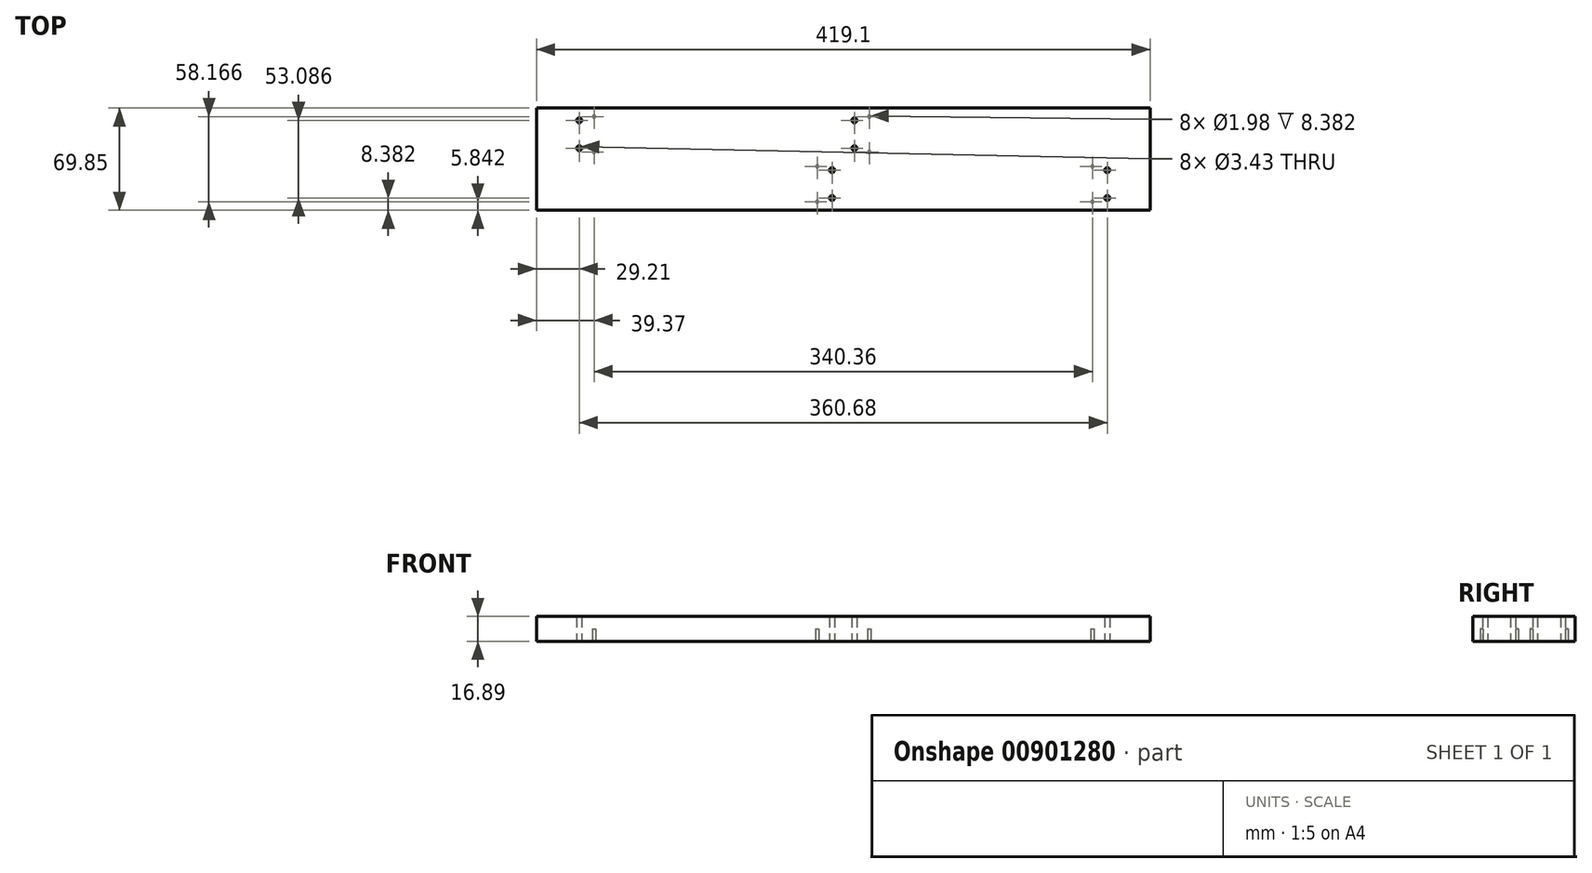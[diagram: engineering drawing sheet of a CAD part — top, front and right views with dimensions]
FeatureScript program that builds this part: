
annotation { "Feature Type Name" : "Feature", "Feature Type Description" : "" }
export const myFeature = defineFeature(function(context is Context, id is Id, definition is map)
    precondition{}
    {
        {
            var Q0;
            Q0=qCreatedBy(makeId("Top.planeOp"),FACE);
            var sketch = newSketch(context, id + "F0", { "sketchPlane" : qUnion([Q0])});
            skLineSegment(sketch, "E0.bottom", {"start": v(0, 0) * mm, "end": v(419.1, 0) * mm});
            skLineSegment(sketch, "E0.top", {"start": v(0, 69.85) * mm, "end": v(419.1, 69.85) * mm});
            skLineSegment(sketch, "E0.left", {"start": v(0, 0) * mm, "end": v(0, 69.85) * mm});
            skLineSegment(sketch, "E0.right", {"start": v(419.1, 0) * mm, "end": v(419.1, 69.85) * mm});
            skSolve(sketch);
        }
        {
            var Q0;
            Q0=qSketchRegion(id+"F0",true);
            extrude(context, id + "F1", {"entities" : qUnion([Q0]), "depth" : 16.9 * mm, "offsetDistance" : 25.4 * mm});
        }
        {
            var Q0;
            Q0=makeQuery(id+"F1.opExtrude","CAP_FACE",FACE,{"disambiguationData":[OSD([sQuery(id+"F0.wireOp",EDGE,"E0.bottom"),sQuery(id+"F0.wireOp",EDGE,"E0.top"),sQuery(id+"F0.wireOp",EDGE,"E0.left"),sQuery(id+"F0.wireOp",EDGE,"E0.right")])],"isStart":true});
            var sketch = newSketch(context, id + "F2", { "sketchPlane" : qUnion([Q0])});
            skCircle(sketch, "E1", {"center": v(379.73, -5.84) * mm, "radius": 1 * mm});
            skCircle(sketch, "E2", {"center": v(379.73, -29.97) * mm, "radius": 1 * mm});
            skCircle(sketch, "E3", {"center": v(227.33, -39.88) * mm, "radius": 1 * mm});
            skCircle(sketch, "E4", {"center": v(227.33, -64) * mm, "radius": 1 * mm});
            skCircle(sketch, "E5.1.0.0", {"center": v(39.37, -64) * mm, "radius": 1 * mm});
            skCircle(sketch, "E5.1.0.1", {"center": v(191.77, -29.97) * mm, "radius": 1 * mm});
            skCircle(sketch, "E5.1.0.2", {"center": v(39.37, -39.88) * mm, "radius": 1 * mm});
            skCircle(sketch, "E5.1.0.3", {"center": v(191.77, -5.84) * mm, "radius": 1 * mm});
            skLineSegment(sketch, "E5.direction1", {"start": v(227.33, -64) * mm, "end": v(39.37, -64) * mm, "construction": true});
            skSolve(sketch);
        }
        {
            var Q0;
            Q0=qSketchRegion(id+"F2",true);
            extrude(context, id + "F3", {"entities" : qUnion([Q0]), "operationType" : NewBodyOperationType.REMOVE, "oppositeDirection" : true, "depth" : 8.38 * mm, "offsetDistance" : 25.4 * mm});
        }
        {
            var Q0;
            Q0=makeQuery(id+"F1.opExtrude","CAP_FACE",FACE,{"disambiguationData":[OSD([sQuery(id+"F0.wireOp",EDGE,"E0.bottom"),sQuery(id+"F0.wireOp",EDGE,"E0.top"),sQuery(id+"F0.wireOp",EDGE,"E0.left"),sQuery(id+"F0.wireOp",EDGE,"E0.right")])],"isStart":true});
            var sketch = newSketch(context, id + "F4", { "sketchPlane" : qUnion([Q0])});
            skPoint(sketch, "E6", {"position": v(379.73, -5.84) * mm});
            skPoint(sketch, "E7", {"position": v(379.73, -29.97) * mm});
            skPoint(sketch, "E8", {"position": v(227.33, -39.88) * mm});
            skPoint(sketch, "E9", {"position": v(227.33, -64) * mm});
            skCircle(sketch, "E10", {"center": v(389.9, -8.38) * mm, "radius": 1.71 * mm});
            skCircle(sketch, "E11", {"center": v(389.9, -27.43) * mm, "radius": 1.71 * mm});
            skCircle(sketch, "E12", {"center": v(217.17, -42.42) * mm, "radius": 1.71 * mm});
            skCircle(sketch, "E13", {"center": v(217.17, -61.47) * mm, "radius": 1.71 * mm});
            skPoint(sketch, "E14.1.0.0", {"position": v(39.37, -39.88) * mm});
            skCircle(sketch, "E14.1.0.1", {"center": v(29.2, -42.42) * mm, "radius": 1.71 * mm});
            skPoint(sketch, "E14.1.0.2", {"position": v(191.77, -5.84) * mm});
            skCircle(sketch, "E14.1.0.3", {"center": v(29.2, -61.47) * mm, "radius": 1.71 * mm});
            skPoint(sketch, "E14.1.0.4", {"position": v(39.37, -64) * mm});
            skPoint(sketch, "E14.1.0.5", {"position": v(191.77, -29.97) * mm});
            skCircle(sketch, "E14.1.0.6", {"center": v(201.93, -27.43) * mm, "radius": 1.71 * mm});
            skCircle(sketch, "E14.1.0.7", {"center": v(201.93, -8.38) * mm, "radius": 1.71 * mm});
            skLineSegment(sketch, "E14.direction1", {"start": v(227.33, -64) * mm, "end": v(39.37, -64) * mm, "construction": true});
            skPoint(sketch, "E15.1.0.0", {"position": v(-163.83, -64) * mm});
            skPoint(sketch, "E15.1.0.1", {"position": v(-163.83, -39.88) * mm});
            skCircle(sketch, "E15.1.0.2", {"center": v(-174, -42.42) * mm, "radius": 1.71 * mm});
            skCircle(sketch, "E15.1.0.3", {"center": v(-174, -61.47) * mm, "radius": 1.71 * mm});
            skPoint(sketch, "E15.2.0.0", {"position": v(-367.03, -64) * mm});
            skPoint(sketch, "E15.2.0.1", {"position": v(-367.03, -39.88) * mm});
            skCircle(sketch, "E15.2.0.2", {"center": v(-377.2, -42.42) * mm, "radius": 1.71 * mm});
            skCircle(sketch, "E15.2.0.3", {"center": v(-377.2, -61.47) * mm, "radius": 1.71 * mm});
            skLineSegment(sketch, "E15.direction1", {"start": v(39.37, -64) * mm, "end": v(-163.83, -64) * mm, "construction": true});
            skSolve(sketch);
        }
        {
            var Q0;
            Q0=qSketchRegion(id+"F4",true);
            extrude(context, id + "F5", {"entities" : qUnion([Q0]), "operationType" : NewBodyOperationType.REMOVE, "oppositeDirection" : true, "depth" : 25.4 * mm, "offsetDistance" : 25.4 * mm});
        }
    });
